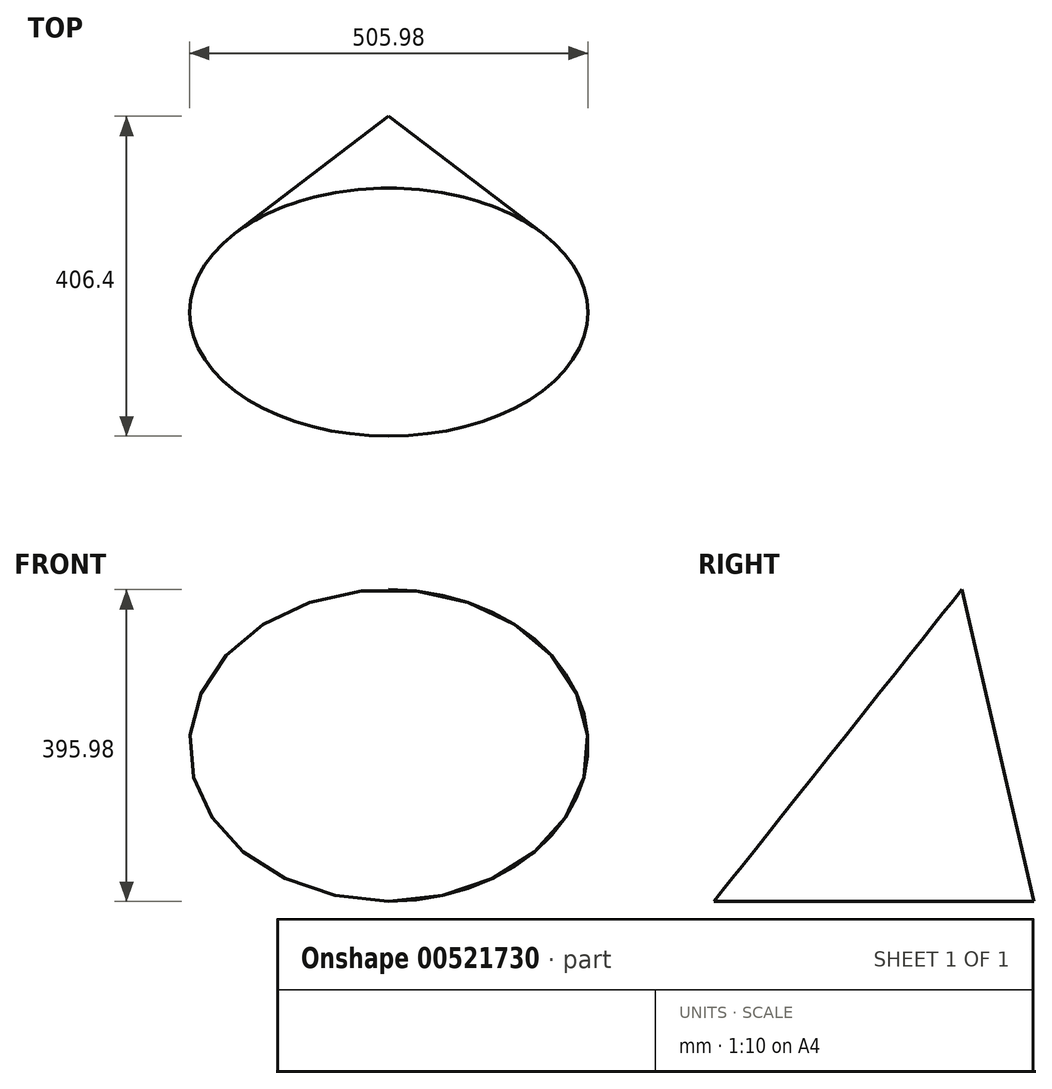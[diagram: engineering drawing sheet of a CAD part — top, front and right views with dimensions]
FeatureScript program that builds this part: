
annotation { "Feature Type Name" : "Feature", "Feature Type Description" : "" }
export const myFeature = defineFeature(function(context is Context, id is Id, definition is map)
    precondition{}
    {
        {
            var Q0;
            Q0=qCreatedBy(makeId("Right.planeOp"),FACE);
            var sketch = newSketch(context, id + "F0", { "sketchPlane" : qUnion([Q0])});
            skLineSegment(sketch, "E0", {"start": v(0, 0) * mm, "end": v(-406.4, 0) * mm});
            skLineSegment(sketch, "E1", {"start": v(0, 0) * mm, "end": v(-248.91, 198) * mm});
            skLineSegment(sketch, "E2", {"start": v(-248.91, 198) * mm, "end": v(-406.4, 0) * mm});
            skSolve(sketch);
        }
        {
            var Q0;
            Q0 = qSketchRegion(id + "F0", true);
            var Q1;
            Q1=sQuery(id+"F0.wireOp",EDGE,"E1");
            revolve(context, id + "F1", {"entities" : qUnion([Q0]), "axis" : qUnion([Q1]), "revolveType" : RevolveType.FULL});
        }
        {
            var Q0;
            Q0=makeQuery(id+"F1.opRevolve","SWEPT_FACE",FACE,{"disambiguationData":[OSD([sQuery(id+"F0.wireOp",EDGE,"E2")])]});
            var sketch = newSketch(context, id + "F2", { "sketchPlane" : qUnion([Q0])});
            skLineSegment(sketch, "E3", {"start": v(-207.1, -145.3) * mm, "end": v(207.1, -145.3) * mm});
            skSolve(sketch);
        }
        {
            var Q0;
            Q0=qCreatedBy(makeId("Top.planeOp"),FACE);
            var sketch = newSketch(context, id + "F3", { "sketchPlane" : qUnion([Q0])});
            skLineSegment(sketch, "E4", {"start": v(-207.15, -339.4) * mm, "end": v(222.17, -339.4) * mm});
            skSolve(sketch);
        }
        {
            var Q0;
            Q0=sQuery(id+"F2.wireOp",VERTEX,"E3.end");
            var Q1;
            Q1=sQuery(id+"F3.wireOp",VERTEX,"E4.end");
            var Q2;
            Q2=sQuery(id+"F3.wireOp",VERTEX,"E4.start");
            cPlane(context, id + "F4", {"entities" : qUnion([Q0, Q1, Q2]), "cplaneType" : CPlaneType.THREE_POINT, "offset" : 25.4 * mm, "width" : 152.4 * mm, "height" : 152.4 * mm});
        }
    });
